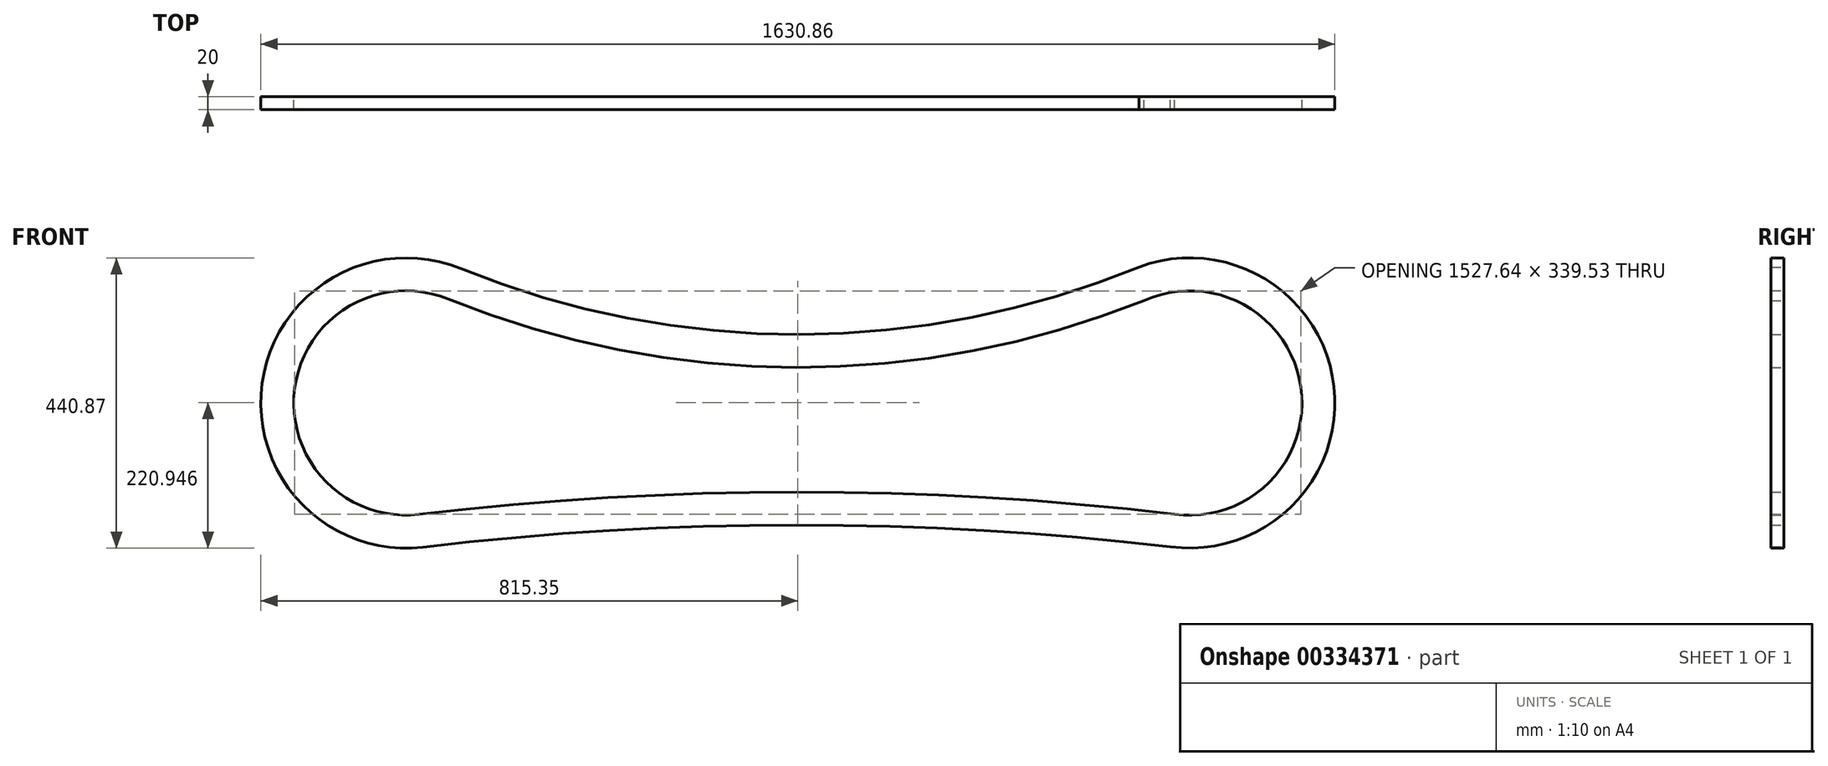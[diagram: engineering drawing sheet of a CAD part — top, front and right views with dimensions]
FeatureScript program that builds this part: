
annotation { "Feature Type Name" : "Feature", "Feature Type Description" : "" }
export const myFeature = defineFeature(function(context is Context, id is Id, definition is map)
    precondition{}
    {
        {
            var Q0;
            Q0=qCreatedBy(makeId("Front.planeOp"),FACE);
            var sketch = newSketch(context, id + "F0", { "sketchPlane" : qUnion([Q0])});
            skArc(sketch, "E0", {"start": v(-511.1, 185.67) * mm, "mid": v(-812.57, 10.99) * mm, "end": v(-568.25, -237.43) * mm});
            skArc(sketch, "E1", {"start": v(566.36, -236.97) * mm, "mid": v(814.94, 6.03) * mm, "end": v(518.72, 187.97) * mm});
            skArc(sketch, "E2", {"start": v(566.36, -236.97) * mm, "mid": v(-0.96, -203.9) * mm, "end": v(-568.25, -237.43) * mm});
            skPoint(sketch, "E2.centerSnap0", {"position": v(1.02, -2.46) * mm});
            skArc(sketch, "E3", {"start": v(-511.1, 185.67) * mm, "mid": v(4.04, 85.55) * mm, "end": v(518.72, 187.97) * mm});
            skArc(sketch, "E4.0", {"start": v(-529.92, 139.36) * mm, "mid": v(-763.02, 4.3) * mm, "end": v(-574.12, -187.78) * mm});
            skArc(sketch, "E4.1", {"start": v(-529.92, 139.36) * mm, "mid": v(-1.9, 35.54) * mm, "end": v(526.55, 137.17) * mm});
            skArc(sketch, "E4.2", {"start": v(572.65, -187.37) * mm, "mid": v(764.62, 5.45) * mm, "end": v(526.55, 137.17) * mm});
            skArc(sketch, "E4.3", {"start": v(572.65, -187.37) * mm, "mid": v(-0.74, -153.9) * mm, "end": v(-574.12, -187.78) * mm});
            skSolve(sketch);
        }
        {
            var Q0;
            Q0=makeQuery(id+"F0.imprint","IMPRINT",FACE,{"disambiguationData":[TD([[makeQuery(id+"F0.imprint","IMPRINT",EDGE,{"derivedFrom":sQuery(id+"F0.wireOp",EDGE,"E0")}),1.0]])]});
            extrude(context, id + "F1", {"entities" : qUnion([Q0]), "depth" : 20 * mm});
        }
    });
